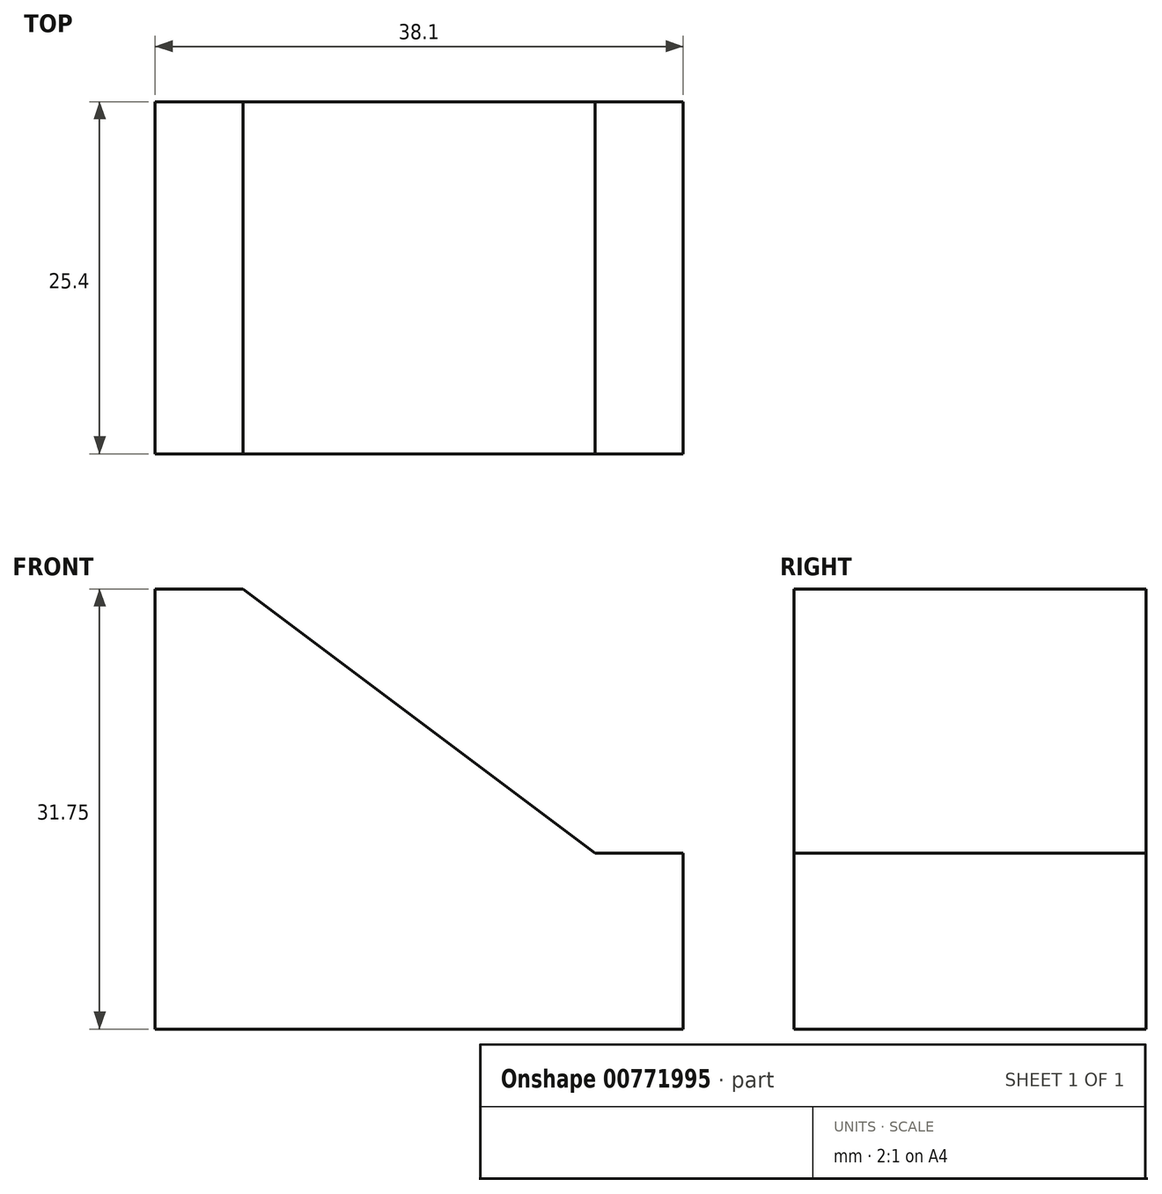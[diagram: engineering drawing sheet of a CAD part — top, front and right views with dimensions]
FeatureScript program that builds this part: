
annotation { "Feature Type Name" : "Feature", "Feature Type Description" : "" }
export const myFeature = defineFeature(function(context is Context, id is Id, definition is map)
    precondition{}
    {
        {
            var Q0;
            Q0=qCreatedBy(makeId("Front.planeOp"),FACE);
            var sketch = newSketch(context, id + "F0", { "sketchPlane" : qUnion([Q0])});
            skLineSegment(sketch, "E0", {"start": v(0, 0) * mm, "end": v(0, -31.75) * mm});
            skLineSegment(sketch, "E1", {"start": v(0, -31.75) * mm, "end": v(38.1, -31.75) * mm});
            skLineSegment(sketch, "E2", {"start": v(38.1, -31.75) * mm, "end": v(38.1, -19.05) * mm});
            skLineSegment(sketch, "E3", {"start": v(38.1, -19.05) * mm, "end": v(31.75, -19.05) * mm});
            skLineSegment(sketch, "E4", {"start": v(0, 0) * mm, "end": v(6.35, 0) * mm});
            skLineSegment(sketch, "E5", {"start": v(6.35, 0) * mm, "end": v(31.75, -19.05) * mm});
            skSolve(sketch);
        }
        {
            var Q0;
            Q0 = qSketchRegion(id + "F0", true);
            extrude(context, id + "F1", {"entities" : qUnion([Q0]), "depth" : 25.4 * mm, "offsetDistance" : 25.4 * mm});
        }
    });
